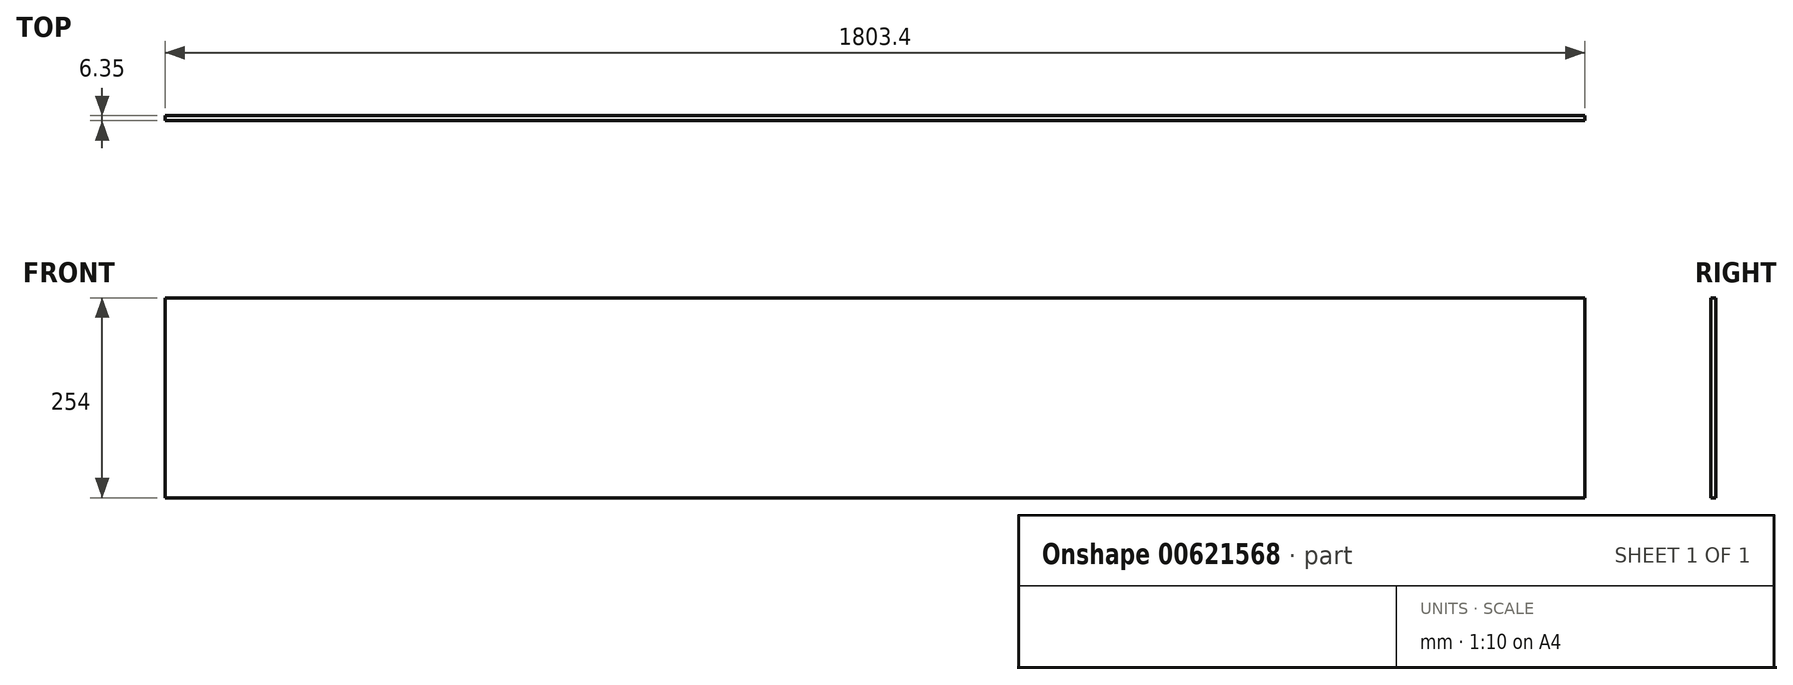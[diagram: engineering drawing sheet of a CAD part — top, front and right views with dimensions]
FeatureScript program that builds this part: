
annotation { "Feature Type Name" : "Feature", "Feature Type Description" : "" }
export const myFeature = defineFeature(function(context is Context, id is Id, definition is map)
    precondition{}
    {
        {
            var Q0;
            Q0=qCreatedBy(makeId("Front.planeOp"),FACE);
            var sketch = newSketch(context, id + "F0", { "sketchPlane" : qUnion([Q0])});
            skLineSegment(sketch, "E0.bottom", {"start": v(901.7, 127) * mm, "end": v(-901.7, 127) * mm});
            skLineSegment(sketch, "E0.top", {"start": v(901.7, -127) * mm, "end": v(-901.7, -127) * mm});
            skLineSegment(sketch, "E0.left", {"start": v(901.7, 127) * mm, "end": v(901.7, -127) * mm});
            skLineSegment(sketch, "E0.right", {"start": v(-901.7, 127) * mm, "end": v(-901.7, -127) * mm});
            skPoint(sketch, "E0.middle", {"position": v(0, 0) * mm});
            skSolve(sketch);
        }
        {
            var Q0;
            Q0 = qSketchRegion(id + "F0", true);
            extrude(context, id + "F1", {"entities" : qUnion([Q0]), "depth" : 6.35 * mm, "offsetDistance" : 25.4 * mm});
        }
    });
